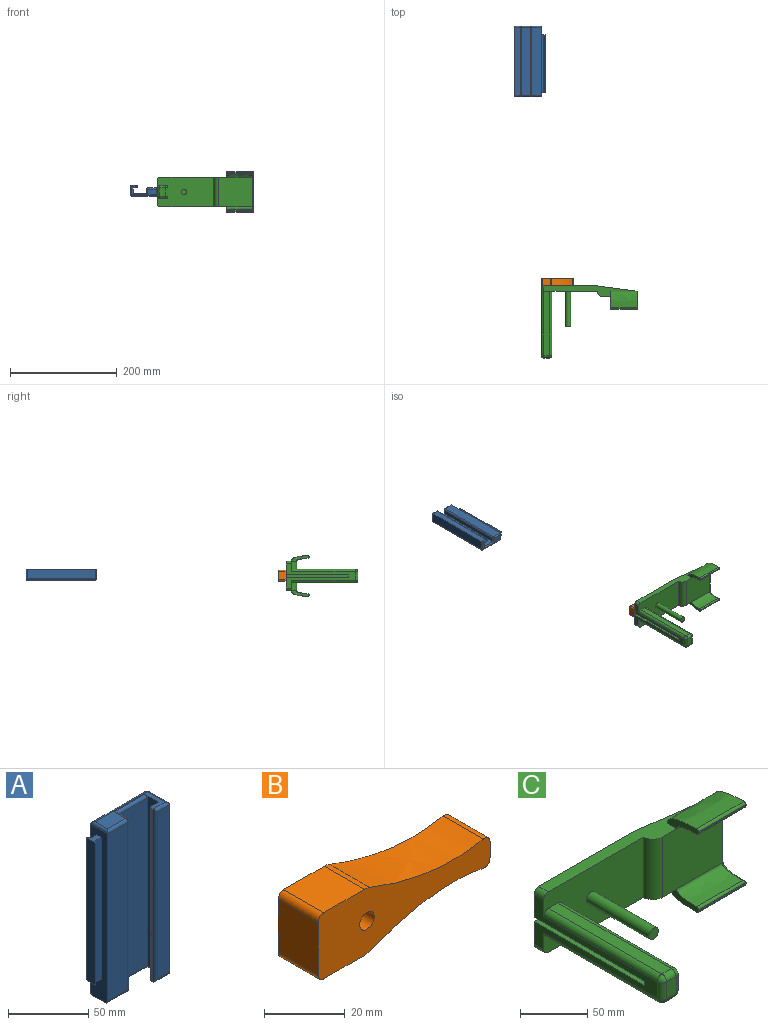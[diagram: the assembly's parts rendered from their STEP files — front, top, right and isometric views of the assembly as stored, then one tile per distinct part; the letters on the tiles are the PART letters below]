
ASSEMBLY  parts=3 mates=2
PART A: 42 faces, bbox 57.1x20x132 mm
  f0: plane 47.96x16mm, normal (0,0,-1), area 252.6mm2, adj f8,f14,f18,f19,f20,f29,f31,f34
  f1: plane 108.71x8.24mm, normal (-1,0,0), area 896.1mm2, adj f4,f5,f17,f41
  f2: plane 108.71x5mm, normal (0,-1,0), area 543.6mm2, adj f5,f8,f17,f41
  f3: plane 108.71x5mm, normal (0,1,0), area 543.6mm2, adj f4,f8,f17,f41
  f4: plane 108.71x2.12mm, normal (0.71,0.71,0), area 326.1mm2, adj f1,f3,f17,f41
  f5: plane 108.71x2.12mm, normal (0.71,-0.71,0), area 326.1mm2, adj f1,f2,f17,f41
  f6: plane 45.96x16mm, normal (0,0,1), area 273.7mm2, adj f12,f13,f14,f21,f22,f23,f26,f27
  f7: plane 128x47.96mm, normal (0,1,0), area 6138.8mm2, adj f8,f28,f34,f36
  f8: plane 130x15mm, normal (-1,0,0), area 1513.4mm2, adj f0,f2,f3,f7,f9,f17,f27,f34
  f9: plane 128x17.96mm, normal (0,-1,0), area 2298.8mm2, adj f8,f24,f26,f38
  f10: plane 128x8mm, normal (1,0,0), area 1024mm2, adj f11,f23,f24,f40
  f11: plane 128x25mm, normal (0,-1,0), area 3200mm2, adj f10,f12,f18,f22
  f12: plane 130x12mm, normal (-1,0,0), area 1300.9mm2, adj f6,f11,f13,f19,f22
  f13: plane 130x6.01mm, normal (0,1,0), area 781.7mm2, adj f6,f12,f20,f21
  f14: plane 132x1mm, normal (-1,0,0), area 132mm2, adj f0,f6,f21,f33
  f15: plane 128x11.01mm, normal (0,-1,0), area 1409.7mm2, adj f16,f31,f32,f33
  f16: plane 128x18mm, normal (1,0,0), area 2304mm2, adj f15,f29,f30,f36
  f17: plane 8.24x7.12mm, normal (0,0,1), area 33mm2, adj f1,f2,f3,f4,f5,f8
  f18: cylinder r=2mm len=29mm, axis (-1,0,0), area 83.1mm2, adj f0,f11,f19,f40
  f19: cylinder r=2mm len=14mm, axis (0,1,0), area 36mm2, adj f0,f12,f18,f20
  f20: cylinder r=2mm len=10.01mm, axis (1,0,0), area 25.2mm2, adj f0,f13,f19,f21
  f21: cylinder r=2mm len=132mm, axis (0,0,1), area 412.4mm2, adj f6,f13,f14,f20
  f22: cylinder r=2mm len=27mm, axis (1,0,0), area 80.8mm2, adj f6,f11,f12,f23
  f23: cylinder r=2mm len=10mm, axis (0,-1,0), area 27.4mm2, adj f6,f10,f22,f25
  f24: cylinder r=2mm len=128mm, axis (0,0,1), area 402.1mm2, adj f9,f10,f25,f39
  f25: sphere r=2mm, area 6.3mm2, adj f23,f24,f26
  f26: cylinder r=2mm len=17.96mm, axis (-1,0,0), area 54.1mm2, adj f6,f9,f25,f27
  f27: cylinder r=2mm len=15mm, axis (0,1,0), area 42.6mm2, adj f6,f8,f26,f28
  f28: cylinder r=2mm len=47.96mm, axis (1,0,0), area 148.4mm2, adj f6,f7,f27,f37
  f29: cylinder r=2mm len=18mm, axis (0,-1,0), area 54.3mm2, adj f0,f16,f31,f35
  f30: cylinder r=2mm len=18mm, axis (0,1,0), area 54.3mm2, adj f6,f16,f32,f37
  f31: cylinder r=2mm len=13.01mm, axis (-1,0,0), area 36.3mm2, adj f0,f15,f29,f33
  f32: cylinder r=2mm len=13.01mm, axis (1,0,0), area 36.3mm2, adj f6,f15,f30,f33
  f33: cylinder r=2mm len=132mm, axis (0,0,-1), area 410.1mm2, adj f14,f15,f31,f32
  f34: cylinder r=2mm len=47.96mm, axis (-1,0,0), area 150.7mm2, adj f0,f7,f8,f35
  f35: sphere r=2mm, area 6.3mm2, adj f29,f34,f36
  f36: cylinder r=2mm len=128mm, axis (0,0,-1), area 402.1mm2, adj f7,f16,f35,f37
  f37: sphere r=2mm, area 6.3mm2, adj f28,f30,f36
  f38: cylinder r=2mm len=17.96mm, axis (1,0,0), area 56.4mm2, adj f0,f8,f9,f39
  f39: sphere r=2mm, area 6.3mm2, adj f24,f38,f40
  f40: cylinder r=2mm len=10mm, axis (0,1,0), area 27.4mm2, adj f0,f10,f18,f39
  f41: plane 8.24x7.12mm, normal (0,0,-1), area 33mm2, adj f1,f2,f3,f4,f5,f8
PART B: 16 faces, bbox 60.1x14x20 mm
  f0: plane 60.09x20mm, normal (0,1,0), area 776.8mm2, adj f2,f3,f4,f7,f8,f9,f10,f11
  f1: plane 60.09x20mm, normal (0,-1,0), area 756.4mm2, adj f2,f3,f4,f5,f7,f8,f9,f10
  f2: plane 14x4.92mm, normal (1,0,0), area 68.9mm2, adj f0,f1,f9,f10
  f3: plane 14.11x14mm, normal (0,0,1), area 197.6mm2, adj f0,f1,f12,f15
  f4: plane 14.11x14mm, normal (0,0,-1), area 197.6mm2, adj f0,f1,f13,f14
  f5: cylinder r=2.55mm len=5.1mm, axis (0,-1,0), area 80.1mm2, adj f1,f6
  f6: plane 5.1x5.1mm, normal (0,-1,0), area 20.4mm2, adj f5
  f7: extruded ~39.7x14mm, area 568.8mm2, adj f0,f1,f10,f15
  f8: extruded ~39.7x14mm, area 568.8mm2, adj f0,f1,f9,f14
  f9: cylinder r=2mm len=14mm, axis (0,1,0), area 49.9mm2, adj f0,f1,f2,f8
  f10: cylinder r=2mm len=14mm, axis (0,1,0), area 49.9mm2, adj f0,f1,f2,f7
  f11: plane 16x14mm, normal (-1,0,0), area 224mm2, adj f0,f1,f12,f13
  f12: cylinder r=2mm len=14mm, axis (0,1,0), area 44mm2, adj f0,f1,f3,f11
  f13: cylinder r=2mm len=14mm, axis (0,-1,0), area 44mm2, adj f0,f1,f4,f11
  f14: cylinder r=5mm len=14mm, axis (0,1,0), area 26.6mm2, adj f0,f1,f4,f8
  f15: cylinder r=5mm len=14mm, axis (0,1,0), area 26.6mm2, adj f0,f1,f3,f7
PART C: 53 faces, bbox 180x139.6x76.1 mm
  f0: plane 173.94x20mm, normal (0,0,1), area 1603.2mm2, adj f3,f15,f19,f21,f26,f28,f30,f32
  f1: plane 119.58x9.96mm, normal (0,0,-1), area 1191mm2, adj f15,f35,f40,f41
  f2: plane 119.58x9.96mm, normal (0,0,1), area 1191mm2, adj f15,f33,f38,f39
  f3: plane 104.98x55mm, normal (0,1,0), area 5710.5mm2, adj f0,f5,f7,f9,f10,f11,f12,f13
  f4: plane 119.58x15mm, normal (1,0,0), area 1793.7mm2, adj f15,f33,f34,f35
  f5: plane 129.58x45mm, normal (-1,0,0), area 1776.5mm2, adj f3,f9,f13,f14,f15,f31,f32,f38
  f6: plane 15x9.96mm, normal (0,-1,0), area 149.4mm2, adj f34,f39,f40,f44
  f7: cylinder r=2.5mm len=5mm, axis (0,-1,0), area 78.5mm2, adj f3,f8
  f8: plane 5x5mm, normal (0,1,0), area 19.6mm2, adj f7
  f9: plane 116.8x5mm, normal (0,0,-1), area 584mm2, adj f3,f5,f10,f14
  f10: plane 116.8x2.12mm, normal (0.71,0,-0.71), area 350.4mm2, adj f3,f9,f11,f14
  f11: plane 116.8x8.24mm, normal (-1,0,0), area 962.7mm2, adj f3,f10,f12,f14
  f12: plane 116.8x2.12mm, normal (0.71,0,0.71), area 350.4mm2, adj f3,f11,f13,f14
  f13: plane 116.8x5mm, normal (0,0,1), area 584mm2, adj f3,f5,f12,f14
  f14: plane 8.24x7.12mm, normal (0,1,0), area 33mm2, adj f5,f9,f10,f11,f12,f13
  f15: plane 104.98x55mm, normal (0,-1,0), area 5207mm2, adj f0,f1,f2,f4,f5,f16,f18,f30
  f16: cylinder r=5mm len=66mm, axis (0,1,0), area 2073.5mm2, adj f15,f17
  f17: plane 10x10mm, normal (0,-1,0), area 78.5mm2, adj f16
  f18: plane 173.94x20mm, normal (0,0,-1), area 1603.2mm2, adj f3,f15,f19,f21,f23,f24,f30,f31
  f19: plane 63x55mm, normal (0,-1,0), area 3465mm2, adj f0,f18,f25,f27,f30,f47
  f20: plane 76.06x33.12mm, normal (1,0,0), area 594.8mm2, adj f22,f24,f28,f29,f46,f47,f49,f50
  f21: plane 73.26x55mm, normal (0.13,0.99,0), area 4065.2mm2, adj f0,f3,f18,f52
  f22: plane 50x1.01mm, normal (0,-1,0), area 50.4mm2, adj f20,f23,f48,f49,f51
  f23: plane 33.11x10.53mm, normal (-1,0,0), area 183mm2, adj f18,f22,f24,f25,f48,f51
  f24: extruded ~50x31.09mm, area 1763.7mm2, adj f18,f20,f23,f51,f52
  f25: extruded ~48x21.14mm, area 1106.2mm2, adj f19,f23,f48,f49
  f26: plane 33.11x10.53mm, normal (-1,0,0), area 183mm2, adj f0,f27,f28,f29,f45,f50
  f27: extruded ~48x21.14mm, area 1106.2mm2, adj f19,f26,f45,f46
  f28: extruded ~50x31.09mm, area 1763.7mm2, adj f0,f20,f26,f50,f52
  f29: plane 50x1.01mm, normal (0,-1,0), area 50.4mm2, adj f20,f26,f45,f46,f50
  f30: cylinder r=10mm len=55mm, axis (0,0,-1), area 863.9mm2, adj f0,f15,f18,f19
  f31: cylinder r=5mm len=10mm, axis (0,-1,0), area 78.5mm2, adj f3,f5,f15,f18
  f32: cylinder r=5mm len=10mm, axis (0,-1,0), area 78.5mm2, adj f0,f3,f5,f15
  f33: cylinder r=5mm len=119.58mm, axis (0,-1,0), area 939.2mm2, adj f2,f4,f15,f36
  f34: cylinder r=5mm len=15mm, axis (0,0,1), area 117.8mm2, adj f4,f6,f36,f37
  f35: cylinder r=5mm len=119.58mm, axis (0,1,0), area 939.2mm2, adj f1,f4,f15,f37
  f36: sphere r=5mm, area 39.3mm2, adj f33,f34,f39
  f37: sphere r=5mm, area 39.3mm2, adj f34,f35,f40
  f38: cylinder r=5mm len=119.58mm, axis (0,1,0), area 939.2mm2, adj f2,f5,f15,f42
  f39: cylinder r=5mm len=9.96mm, axis (-1,0,0), area 78.2mm2, adj f2,f6,f36,f42
  f40: cylinder r=5mm len=9.96mm, axis (1,0,0), area 78.2mm2, adj f1,f6,f37,f43
  f41: cylinder r=5mm len=119.58mm, axis (0,-1,0), area 939.2mm2, adj f1,f5,f15,f43
  f42: sphere r=5mm, area 39.3mm2, adj f38,f39,f44
  f43: sphere r=5mm, area 39.3mm2, adj f40,f41,f44
  f44: cylinder r=5mm len=15mm, axis (0,0,-1), area 117.8mm2, adj f5,f6,f42,f43
  f45: cylinder r=2mm len=50mm, axis (1,0,0), area 152.5mm2, adj f26,f27,f29,f46
  f46: bspline ~26.24x10.11mm, area 79.9mm2, adj f20,f27,f29,f45,f47
  f47: cylinder r=2mm len=55mm, axis (0,0,-1), area 172.8mm2, adj f19,f20,f46,f49
  f48: cylinder r=2mm len=50mm, axis (1,0,0), area 152.5mm2, adj f22,f23,f25,f49
  f49: bspline ~26.24x10.11mm, area 79.9mm2, adj f20,f22,f25,f47,f48
  f50: cylinder r=2mm len=50mm, axis (1,0,0), area 158.1mm2, adj f20,f26,f28,f29
  f51: cylinder r=2mm len=50mm, axis (1,0,0), area 158.1mm2, adj f20,f22,f23,f24
  f52: cylinder r=2mm len=63.57mm, axis (0,0,1), area 169.9mm2, adj f0,f18,f20,f21,f24,f28
PLACE A rot(axis=(0,-0.71,0.71),180deg) t=(-425.33,585.17,-318.13)mm
PLACE B rot(axis=(0,1,0),2.3deg) t=(-404.58,99.13,-227.7)mm
PLACE C t=(-372.4,31.91,-318.13)mm fixed
MATE slider A.f17 <-> C.f14  axis (0,-1,0) through (-411.4,460.29,-318.13)mm
MATE revolute B.f5 <-> C.f7  axis (0,-1,0) through (-398.27,104.13,-318.13)mm
